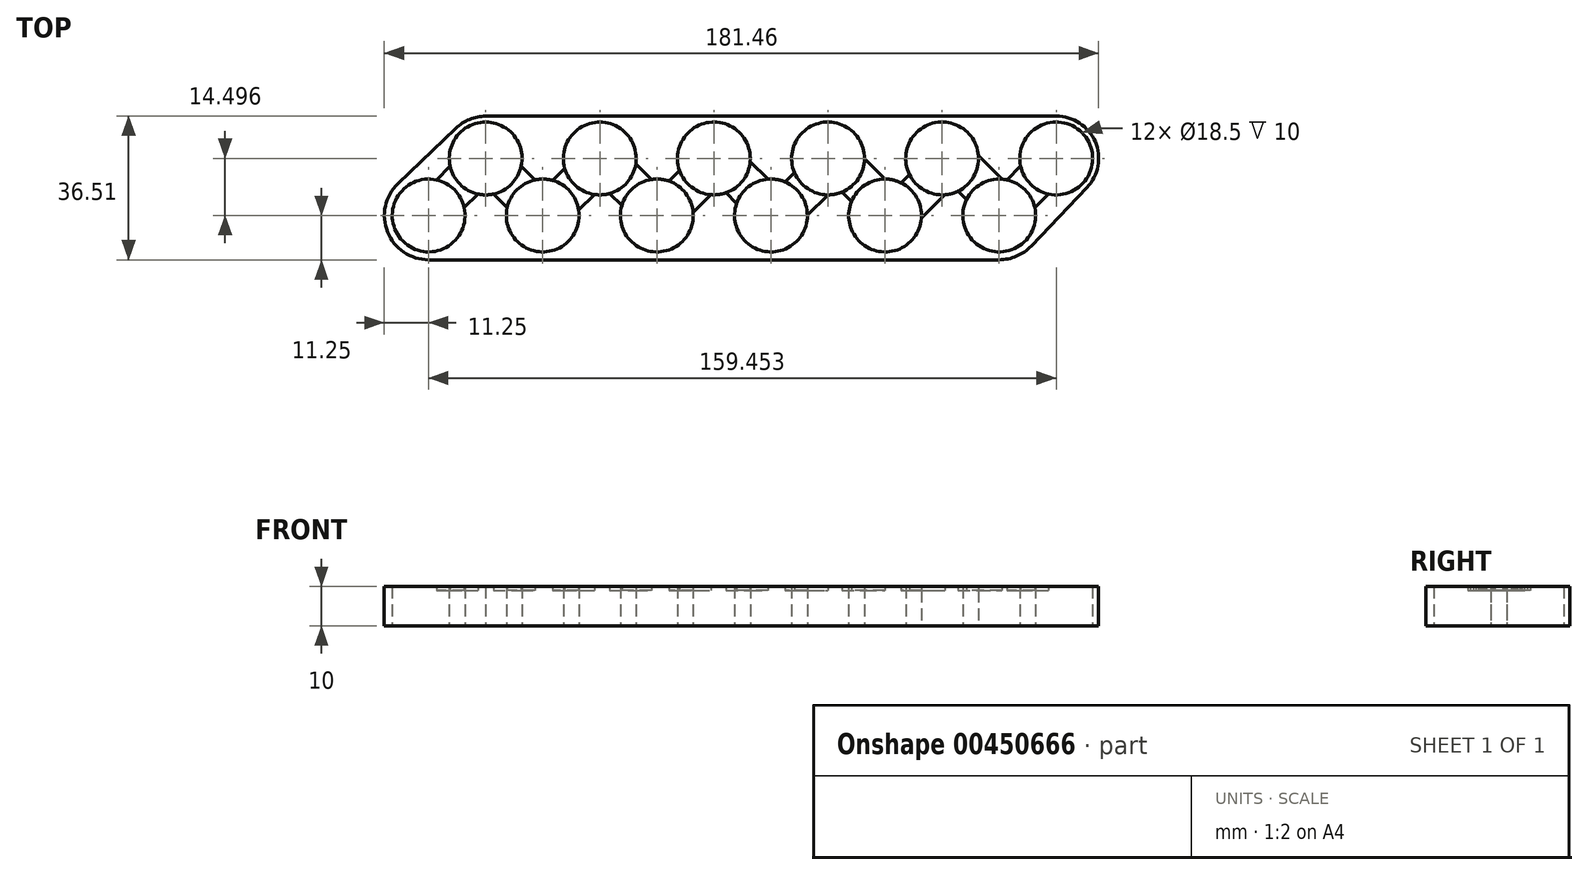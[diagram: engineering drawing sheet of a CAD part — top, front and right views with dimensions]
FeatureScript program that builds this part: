
annotation { "Feature Type Name" : "Feature", "Feature Type Description" : "" }
export const myFeature = defineFeature(function(context is Context, id is Id, definition is map)
    precondition{}
    {
        {
            var Q0;
            Q0=qCreatedBy(makeId("Top.planeOp"),FACE);
            var sketch = newSketch(context, id + "F0", { "sketchPlane" : qUnion([Q0])});
            skCircle(sketch, "E0", {"center": v(0, 0) * mm, "radius": 9.25 * mm});
            skCircle(sketch, "E1", {"center": v(14.5, 14.5) * mm, "radius": 9.25 * mm});
            skLineSegment(sketch, "E2", {"start": v(0, 0) * mm, "end": v(14.5, 0) * mm, "construction": true});
            skLineSegment(sketch, "E3", {"start": v(14.5, 0) * mm, "end": v(14.5, 14.5) * mm, "construction": true});
            skArc(sketch, "E4", {"start": v(-7.77, 8.14) * mm, "mid": v(-10.44, -4.19) * mm, "end": v(0, -11.25) * mm});
            skCircle(sketch, "E5.1.0.0", {"center": v(29, 0) * mm, "radius": 9.25 * mm});
            skCircle(sketch, "E5.1.0.3", {"center": v(43.49, 14.5) * mm, "radius": 9.25 * mm});
            skCircle(sketch, "E5.2.0.0", {"center": v(57.98, 0) * mm, "radius": 9.25 * mm});
            skCircle(sketch, "E5.2.0.3", {"center": v(72.48, 14.5) * mm, "radius": 9.25 * mm});
            skCircle(sketch, "E5.3.0.0", {"center": v(86.97, 0) * mm, "radius": 9.25 * mm});
            skCircle(sketch, "E5.3.0.3", {"center": v(101.47, 14.5) * mm, "radius": 9.25 * mm});
            skCircle(sketch, "E5.4.0.0", {"center": v(115.97, 0) * mm, "radius": 9.25 * mm});
            skCircle(sketch, "E5.4.0.3", {"center": v(130.46, 14.5) * mm, "radius": 9.25 * mm});
            skCircle(sketch, "E5.5.0.0", {"center": v(144.96, 0) * mm, "radius": 9.25 * mm});
            skArc(sketch, "E5.5.0.1", {"start": v(144.96, -11.25) * mm, "mid": v(149.39, -10.34) * mm, "end": v(153.1, -7.76) * mm});
            skArc(sketch, "E5.5.0.2", {"start": v(167.24, 7.07) * mm, "mid": v(169.34, 18.73) * mm, "end": v(159.45, 25.26) * mm});
            skCircle(sketch, "E5.5.0.3", {"center": v(159.45, 14.5) * mm, "radius": 9.25 * mm});
            skLineSegment(sketch, "E5.direction1", {"start": v(0, 0) * mm, "end": v(29, 0) * mm, "construction": true});
            skArc(sketch, "E6.trimOffspring", {"start": v(14.5, 25.26) * mm, "mid": v(10.4, 24.42) * mm, "end": v(6.9, 22.14) * mm});
            skLineSegment(sketch, "E7", {"start": v(0, -11.25) * mm, "end": v(144.96, -11.25) * mm});
            skLineSegment(sketch, "E8", {"start": v(14.5, 14.5) * mm, "end": v(14.5, 25.26) * mm, "construction": true});
            skLineSegment(sketch, "E9", {"start": v(159.45, 14.5) * mm, "end": v(159.45, 25.26) * mm, "construction": true});
            skLineSegment(sketch, "E10", {"start": v(159.45, 25.26) * mm, "end": v(14.5, 25.26) * mm});
            skLineSegment(sketch, "E11", {"start": v(153.1, -7.76) * mm, "end": v(167.24, 7.07) * mm});
            skLineSegment(sketch, "E12", {"start": v(-7.77, 8.14) * mm, "end": v(6.9, 22.14) * mm});
            skSolve(sketch);
        }
        {
            var Q0;
            Q0=makeQuery(id+"F0.imprint","IMPRINT",FACE,{"disambiguationData":[TD([[makeQuery(id+"F0.imprint","IMPRINT",EDGE,{"derivedFrom":sQuery(id+"F0.wireOp",EDGE,"E0")}),-1.0]])]});
            extrude(context, id + "F1", {"entities" : qUnion([Q0]), "depth" : 10 * mm});
        }
        {
            var Q0;
            Q0=makeQuery(id+"F1.opExtrude","CAP_FACE",FACE,{"disambiguationData":[OSD([sQuery(id+"F0.wireOp",EDGE,"E0"),sQuery(id+"F0.wireOp",EDGE,"E1"),sQuery(id+"F0.wireOp",EDGE,"E4"),sQuery(id+"F0.wireOp",EDGE,"E5.1.0.0"),sQuery(id+"F0.wireOp",EDGE,"E5.1.0.3"),sQuery(id+"F0.wireOp",EDGE,"E5.2.0.0"),sQuery(id+"F0.wireOp",EDGE,"E5.2.0.3"),sQuery(id+"F0.wireOp",EDGE,"E5.3.0.0"),sQuery(id+"F0.wireOp",EDGE,"E5.3.0.3"),sQuery(id+"F0.wireOp",EDGE,"E5.4.0.0"),sQuery(id+"F0.wireOp",EDGE,"E5.4.0.3"),sQuery(id+"F0.wireOp",EDGE,"E5.5.0.0"),sQuery(id+"F0.wireOp",EDGE,"E5.5.0.1"),sQuery(id+"F0.wireOp",EDGE,"E5.5.0.2"),sQuery(id+"F0.wireOp",EDGE,"E5.5.0.3"),sQuery(id+"F0.wireOp",EDGE,"E6.trimOffspring"),sQuery(id+"F0.wireOp",EDGE,"E7"),sQuery(id+"F0.wireOp",EDGE,"E10")])],"isStart":false});
            var sketch = newSketch(context, id + "F2", { "sketchPlane" : qUnion([Q0])});
            skLineSegment(sketch, "E13", {"start": v(0, 0) * mm, "end": v(14.5, 14.5) * mm, "construction": true});
            skLineSegment(sketch, "E14", {"start": v(14.5, 14.5) * mm, "end": v(29, 0) * mm, "construction": true});
            skLineSegment(sketch, "E15.0", {"start": v(3.18, -3.89) * mm, "end": v(14.5, 7.42) * mm});
            skLineSegment(sketch, "E16.0", {"start": v(17.85, 18.2) * mm, "end": v(32.7, 3.36) * mm});
            skLineSegment(sketch, "E17.0", {"start": v(-3.89, 3.18) * mm, "end": v(10.96, 18.03) * mm});
            skLineSegment(sketch, "E18.0", {"start": v(14.5, 7.42) * mm, "end": v(25.63, -3.71) * mm});
            skLineSegment(sketch, "E19", {"start": v(-3.89, 3.18) * mm, "end": v(3.18, -3.89) * mm});
            skLineSegment(sketch, "E20", {"start": v(25.63, -3.71) * mm, "end": v(32.7, 3.36) * mm});
            skLineSegment(sketch, "E21", {"start": v(17.85, 18.2) * mm, "end": v(10.96, 18.03) * mm});
            skLineSegment(sketch, "E22.1.0.0", {"start": v(25.8, 3.18) * mm, "end": v(40.66, 18.03) * mm});
            skLineSegment(sketch, "E22.1.0.1", {"start": v(25.8, 3.18) * mm, "end": v(32.88, -3.89) * mm});
            skLineSegment(sketch, "E22.1.0.2", {"start": v(32.88, -3.89) * mm, "end": v(44.2, 7.42) * mm});
            skLineSegment(sketch, "E22.1.0.3", {"start": v(44.2, 7.42) * mm, "end": v(55.33, -3.71) * mm});
            skLineSegment(sketch, "E22.1.0.4", {"start": v(55.33, -3.71) * mm, "end": v(62.4, 3.36) * mm});
            skLineSegment(sketch, "E22.1.0.5", {"start": v(47.55, 18.2) * mm, "end": v(62.4, 3.36) * mm});
            skLineSegment(sketch, "E22.1.0.6", {"start": v(47.55, 18.2) * mm, "end": v(40.66, 18.03) * mm});
            skLineSegment(sketch, "E22.2.0.0", {"start": v(55.5, 3.18) * mm, "end": v(70.36, 18.03) * mm});
            skLineSegment(sketch, "E22.2.0.1", {"start": v(55.5, 3.18) * mm, "end": v(62.58, -3.89) * mm});
            skLineSegment(sketch, "E22.2.0.2", {"start": v(62.58, -3.89) * mm, "end": v(73.9, 7.42) * mm});
            skLineSegment(sketch, "E22.2.0.3", {"start": v(73.9, 7.42) * mm, "end": v(85.03, -3.71) * mm});
            skLineSegment(sketch, "E22.2.0.4", {"start": v(85.03, -3.71) * mm, "end": v(92.1, 3.36) * mm});
            skLineSegment(sketch, "E22.2.0.5", {"start": v(77.25, 18.2) * mm, "end": v(92.1, 3.36) * mm});
            skLineSegment(sketch, "E22.2.0.6", {"start": v(77.25, 18.2) * mm, "end": v(70.36, 18.03) * mm});
            skLineSegment(sketch, "E22.3.0.0", {"start": v(85.2, 3.18) * mm, "end": v(100.06, 18.03) * mm});
            skLineSegment(sketch, "E22.3.0.1", {"start": v(85.2, 3.18) * mm, "end": v(92.28, -3.89) * mm});
            skLineSegment(sketch, "E22.3.0.2", {"start": v(92.28, -3.89) * mm, "end": v(103.6, 7.42) * mm});
            skLineSegment(sketch, "E22.3.0.3", {"start": v(103.6, 7.42) * mm, "end": v(114.73, -3.71) * mm});
            skLineSegment(sketch, "E22.3.0.4", {"start": v(114.73, -3.71) * mm, "end": v(121.8, 3.36) * mm});
            skLineSegment(sketch, "E22.3.0.5", {"start": v(106.95, 18.2) * mm, "end": v(121.8, 3.36) * mm});
            skLineSegment(sketch, "E22.3.0.6", {"start": v(106.95, 18.2) * mm, "end": v(100.06, 18.03) * mm});
            skLineSegment(sketch, "E22.4.0.0", {"start": v(114.9, 3.18) * mm, "end": v(129.75, 18.03) * mm});
            skLineSegment(sketch, "E22.4.0.1", {"start": v(114.9, 3.18) * mm, "end": v(121.98, -3.89) * mm});
            skLineSegment(sketch, "E22.4.0.2", {"start": v(121.98, -3.89) * mm, "end": v(133.29, 7.42) * mm});
            skLineSegment(sketch, "E22.4.0.3", {"start": v(133.29, 7.42) * mm, "end": v(144.43, -3.71) * mm});
            skLineSegment(sketch, "E22.4.0.4", {"start": v(144.43, -3.71) * mm, "end": v(151.5, 3.36) * mm});
            skLineSegment(sketch, "E22.4.0.5", {"start": v(136.65, 18.2) * mm, "end": v(151.5, 3.36) * mm});
            skLineSegment(sketch, "E22.4.0.6", {"start": v(136.65, 18.2) * mm, "end": v(129.75, 18.03) * mm});
            skLineSegment(sketch, "E22.direction1", {"start": v(-3.89, 3.18) * mm, "end": v(25.8, 3.18) * mm, "construction": true});
            skLineSegment(sketch, "E23", {"start": v(144.96, 0) * mm, "end": v(159.45, 14.5) * mm, "construction": true});
            skLineSegment(sketch, "E24.0", {"start": v(141.24, 3.36) * mm, "end": v(156.1, 18.2) * mm});
            skLineSegment(sketch, "E25.0", {"start": v(148.32, -3.71) * mm, "end": v(163.16, 11.14) * mm});
            skLineSegment(sketch, "E26", {"start": v(156.1, 18.2) * mm, "end": v(163.16, 11.14) * mm});
            skLineSegment(sketch, "E27", {"start": v(141.24, 3.36) * mm, "end": v(148.32, -3.71) * mm});
            skSolve(sketch);
        }
        {
            var Q0;
            Q0=qSketchRegion(id+"F2",true);
            extrude(context, id + "F3", {"entities" : qUnion([Q0]), "operationType" : NewBodyOperationType.REMOVE, "oppositeDirection" : true, "depth" : 1 * mm});
        }
    });
